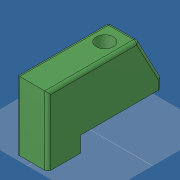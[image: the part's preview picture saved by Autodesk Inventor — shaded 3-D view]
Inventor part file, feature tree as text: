
AUTODESK INVENTOR PART (.ipt)
format: ipt  version: 2019 (Build 230136000, 136)  size: 140,288 bytes
history: native  units: mm
features: extrude x4, sketch x2, fillet x1, other x1
ambient origin geometry x8: Origin, YZ Plane, XZ Plane, XY Plane, X Axis, Y Axis, Z Axis, Center Point
bodies: Volumenkörper1 (feature_tree)
feature tree (8):
  sketch  "Skizze1"  dims[d2=37.0mm d3=10.0mm]
  extrude  "Extrusion1"  Depth=10.0mm
  extrude  "Extrusion5"  Depth=1.0mm TaperAngle=0.0deg
  extrude  "Extrusion3"  Depth=1.0mm TaperAngle=0.0deg
  extrude  "Extrusion6"  Depth=1.0mm
  fillet  "Rundung1"  Radius=7.0mm
  sketch  "Skizze2"  dims[d4=27.5mm d6=22.0mm d7=0.0mm d10=5.0mm d11=0.0mm d14=10.821041mm d15=7.0mm d16=10.0mm d17=0.0mm d18=3.0mm d20=18.0mm d21=11.0mm d22=0.0mm d23=8.0mm d24=8.0mm d25=5.5mm d26=1.0mm]
  other  "Schnittkanten projizieren1"
